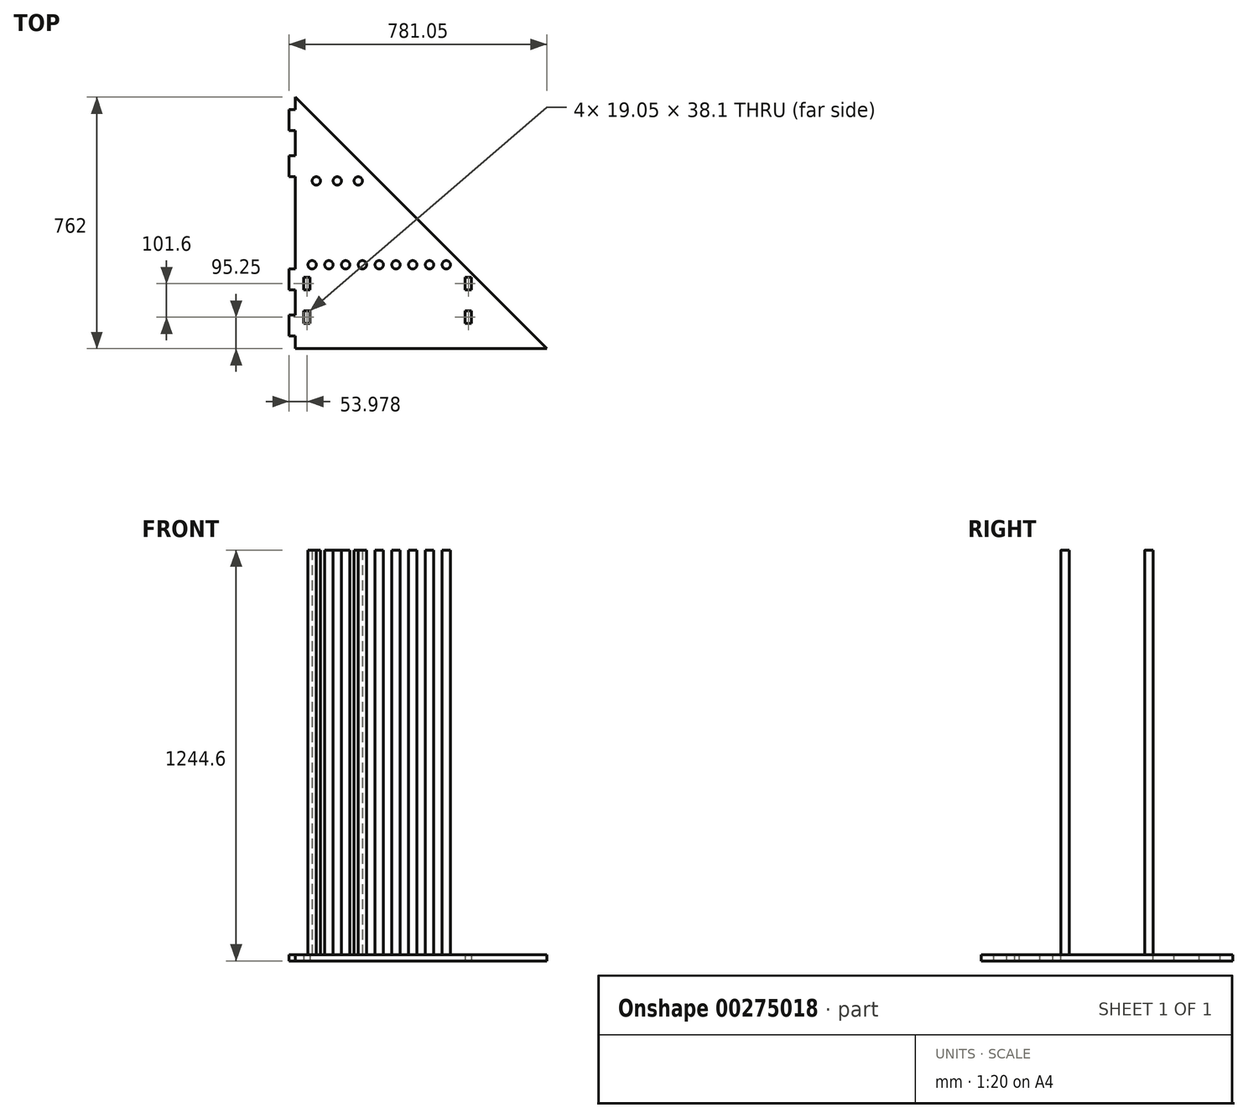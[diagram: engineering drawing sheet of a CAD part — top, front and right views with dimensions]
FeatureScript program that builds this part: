
annotation { "Feature Type Name" : "Feature", "Feature Type Description" : "" }
export const myFeature = defineFeature(function(context is Context, id is Id, definition is map)
    precondition{}
    {
        {
            var Q0;
            Q0=qCreatedBy(makeId("Top.planeOp"),FACE);
            var sketch = newSketch(context, id + "F0", { "sketchPlane" : qUnion([Q0])});
            skLineSegment(sketch, "E0", {"start": v(-270.22, 0) * mm, "end": v(-270.22, -254) * mm});
            skLineSegment(sketch, "E1", {"start": v(-270.22, -254) * mm, "end": v(-270.22, -508) * mm});
            skLineSegment(sketch, "E2", {"start": v(-270.22, -508) * mm, "end": v(-270.22, -762) * mm});
            skLineSegment(sketch, "E3", {"start": v(-270.22, -762) * mm, "end": v(491.78, -762) * mm});
            skLineSegment(sketch, "E4", {"start": v(491.78, -762) * mm, "end": v(-270.22, 0) * mm});
            skLineSegment(sketch, "E5", {"start": v(-270.22, -254) * mm, "end": v(-16.22, -254) * mm});
            skLineSegment(sketch, "E6", {"start": v(-270.22, -508) * mm, "end": v(237.78, -508) * mm});
            skSolve(sketch);
        }
        {
            var Q0;
            Q0 = qSketchRegion(id + "F0", true);
            extrude(context, id + "F1", {"entities" : qUnion([Q0]), "depth" : 19.05 * mm});
        }
        {
            var Q0;
            Q0=makeQuery(id+"F1.opExtrude","CAP_FACE",FACE,{"disambiguationData":[OSD([sQuery(id+"F0.wireOp",EDGE,"E0"),sQuery(id+"F0.wireOp",EDGE,"E1"),sQuery(id+"F0.wireOp",EDGE,"E2"),sQuery(id+"F0.wireOp",EDGE,"E3"),sQuery(id+"F0.wireOp",EDGE,"E4")])],"isStart":false});
            var sketch = newSketch(context, id + "F2", { "sketchPlane" : qUnion([Q0])});
            skPoint(sketch, "E7.centerSnap0", {"position": v(-270.22, -381) * mm});
            skLineSegment(sketch, "E8", {"start": v(-270.22, -508) * mm, "end": v(237.78, -508) * mm});
            skCircle(sketch, "E9", {"center": v(-168.62, -508) * mm, "radius": 12.7 * mm});
            skCircle(sketch, "E10", {"center": v(-67.02, -508) * mm, "radius": 12.7 * mm});
            skCircle(sketch, "E11", {"center": v(34.58, -508) * mm, "radius": 12.7 * mm});
            skCircle(sketch, "E12", {"center": v(136.18, -508) * mm, "radius": 12.7 * mm});
            skCircle(sketch, "E13", {"center": v(-219.42, -508) * mm, "radius": 12.7 * mm});
            skCircle(sketch, "E14", {"center": v(-117.82, -508) * mm, "radius": 12.7 * mm});
            skCircle(sketch, "E15", {"center": v(-16.22, -508) * mm, "radius": 12.7 * mm});
            skCircle(sketch, "E16", {"center": v(85.38, -508) * mm, "radius": 12.7 * mm});
            skCircle(sketch, "E17", {"center": v(186.98, -508) * mm, "radius": 12.7 * mm});
            skLineSegment(sketch, "E18", {"start": v(-270.22, -254) * mm, "end": v(-16.22, -254) * mm});
            skCircle(sketch, "E19", {"center": v(-206.72, -254) * mm, "radius": 12.7 * mm});
            skCircle(sketch, "E20", {"center": v(-143.22, -254) * mm, "radius": 12.7 * mm});
            skCircle(sketch, "E21", {"center": v(-79.72, -254) * mm, "radius": 12.7 * mm});
            skSolve(sketch);
        }
        {
            var Q0;
            Q0 = qSketchRegion(id + "F2", true);
            extrude(context, id + "F3", {"entities" : qUnion([Q0]), "operationType" : NewBodyOperationType.ADD, "depth" : 1225.55 * mm});
        }
        {
            var Q0;
            Q0=makeQuery(id+"F0.imprint","IMPRINT",FACE,{"disambiguationData":[TD([[makeQuery(id+"F0.imprint","IMPRINT",EDGE,{"derivedFrom":sQuery(id+"F0.wireOp",EDGE,"E2")}),1.0]])]});
            var sketch = newSketch(context, id + "F4", { "sketchPlane" : qUnion([Q0])});
            skLineSegment(sketch, "E22.bottom", {"start": v(-225.77, -546.1) * mm, "end": v(-244.82, -546.1) * mm});
            skLineSegment(sketch, "E22.top", {"start": v(-225.77, -584.2) * mm, "end": v(-244.82, -584.2) * mm});
            skLineSegment(sketch, "E22.left", {"start": v(-225.77, -546.1) * mm, "end": v(-225.77, -584.2) * mm});
            skLineSegment(sketch, "E22.right", {"start": v(-244.82, -546.1) * mm, "end": v(-244.82, -584.2) * mm});
            skLineSegment(sketch, "E23.bottom", {"start": v(-225.77, -647.7) * mm, "end": v(-244.82, -647.7) * mm});
            skLineSegment(sketch, "E23.top", {"start": v(-225.77, -685.8) * mm, "end": v(-244.82, -685.8) * mm});
            skLineSegment(sketch, "E23.left", {"start": v(-225.77, -647.7) * mm, "end": v(-225.77, -685.8) * mm});
            skLineSegment(sketch, "E23.right", {"start": v(-244.82, -647.7) * mm, "end": v(-244.82, -685.8) * mm});
            skLineSegment(sketch, "E24.bottom", {"start": v(263.18, -584.2) * mm, "end": v(244.13, -584.2) * mm});
            skLineSegment(sketch, "E24.top", {"start": v(263.18, -546.1) * mm, "end": v(244.13, -546.1) * mm});
            skLineSegment(sketch, "E24.left", {"start": v(263.18, -584.2) * mm, "end": v(263.18, -546.1) * mm});
            skLineSegment(sketch, "E24.right", {"start": v(244.13, -584.2) * mm, "end": v(244.13, -546.1) * mm});
            skLineSegment(sketch, "E25.bottom", {"start": v(263.18, -647.7) * mm, "end": v(244.13, -647.7) * mm});
            skLineSegment(sketch, "E25.top", {"start": v(263.18, -685.8) * mm, "end": v(244.13, -685.8) * mm});
            skLineSegment(sketch, "E25.left", {"start": v(263.18, -647.7) * mm, "end": v(263.18, -685.8) * mm});
            skLineSegment(sketch, "E25.right", {"start": v(244.13, -647.7) * mm, "end": v(244.13, -685.8) * mm});
            skSolve(sketch);
        }
        {
            var Q0;
            Q0 = qSketchRegion(id + "F4", true);
            extrude(context, id + "F5", {"entities" : qUnion([Q0]), "operationType" : NewBodyOperationType.REMOVE, "depth" : 25.4 * mm});
        }
        {
            var Q0;
            Q0=makeQuery(id+"F1.opExtrude","SWEPT_FACE",FACE,{"disambiguationData":[OSD([sQuery(id+"F0.wireOp",EDGE,"E0"),sQuery(id+"F0.wireOp",EDGE,"E1"),sQuery(id+"F0.wireOp",EDGE,"E2")])]});
            var sketch = newSketch(context, id + "F6", { "sketchPlane" : qUnion([Q0])});
            skLineSegment(sketch, "E26", {"start": v(0, 0) * mm, "end": v(381, 0) * mm});
            skLineSegment(sketch, "E27", {"start": v(381, 0) * mm, "end": v(762, 0) * mm});
            skLineSegment(sketch, "E28.bottom", {"start": v(723.9, 0) * mm, "end": v(660.4, 0) * mm});
            skLineSegment(sketch, "E28.top", {"start": v(723.9, 19.05) * mm, "end": v(660.4, 19.05) * mm});
            skLineSegment(sketch, "E28.left", {"start": v(723.9, 0) * mm, "end": v(723.9, 19.05) * mm});
            skLineSegment(sketch, "E28.right", {"start": v(660.4, 0) * mm, "end": v(660.4, 19.05) * mm});
            skLineSegment(sketch, "E29.bottom", {"start": v(584.2, 0) * mm, "end": v(520.7, 0) * mm});
            skLineSegment(sketch, "E29.top", {"start": v(584.2, 19.05) * mm, "end": v(520.7, 19.05) * mm});
            skLineSegment(sketch, "E29.left", {"start": v(584.2, 0) * mm, "end": v(584.2, 19.05) * mm});
            skLineSegment(sketch, "E29.right", {"start": v(520.7, 0) * mm, "end": v(520.7, 19.05) * mm});
            skLineSegment(sketch, "E30.bottom", {"start": v(38.1, 0) * mm, "end": v(101.6, 0) * mm});
            skLineSegment(sketch, "E30.top", {"start": v(38.1, 19.05) * mm, "end": v(101.6, 19.05) * mm});
            skLineSegment(sketch, "E30.left", {"start": v(38.1, 0) * mm, "end": v(38.1, 19.05) * mm});
            skLineSegment(sketch, "E30.right", {"start": v(101.6, 0) * mm, "end": v(101.6, 19.05) * mm});
            skLineSegment(sketch, "E31.bottom", {"start": v(177.8, 0) * mm, "end": v(241.3, 0) * mm});
            skLineSegment(sketch, "E31.top", {"start": v(177.8, 19.05) * mm, "end": v(241.3, 19.05) * mm});
            skLineSegment(sketch, "E31.left", {"start": v(177.8, 0) * mm, "end": v(177.8, 19.05) * mm});
            skLineSegment(sketch, "E31.right", {"start": v(241.3, 0) * mm, "end": v(241.3, 19.05) * mm});
            skSolve(sketch);
        }
        {
            var Q0;
            {Q0=qUnion([makeQuery(id+"F6.imprint","IMPRINT",FACE,{"disambiguationData":[TD([[makeQuery(id+"F6.imprint","IMPRINT",EDGE,{"derivedFrom":sQuery(id+"F6.wireOp",EDGE,"E29.top")}),-1.0]])]}),makeQuery(id+"F6.imprint","IMPRINT",FACE,{"disambiguationData":[TD([[makeQuery(id+"F6.imprint","IMPRINT",EDGE,{"derivedFrom":sQuery(id+"F6.wireOp",EDGE,"E28.top")}),-1.0]])]}),makeQuery(id+"F6.imprint","IMPRINT",FACE,{"disambiguationData":[TD([[makeQuery(id+"F6.imprint","IMPRINT",EDGE,{"derivedFrom":sQuery(id+"F6.wireOp",EDGE,"E30.top")}),-1.0]])]}),makeQuery(id+"F6.imprint","IMPRINT",FACE,{"disambiguationData":[TD([[makeQuery(id+"F6.imprint","IMPRINT",EDGE,{"derivedFrom":sQuery(id+"F6.wireOp",EDGE,"E31.top")}),-1.0]])]})]);}
            extrude(context, id + "F7", {"entities" : qUnion([Q0]), "operationType" : NewBodyOperationType.ADD, "depth" : 19.05 * mm, "offsetDistance" : 25.4 * mm});
        }
    });
